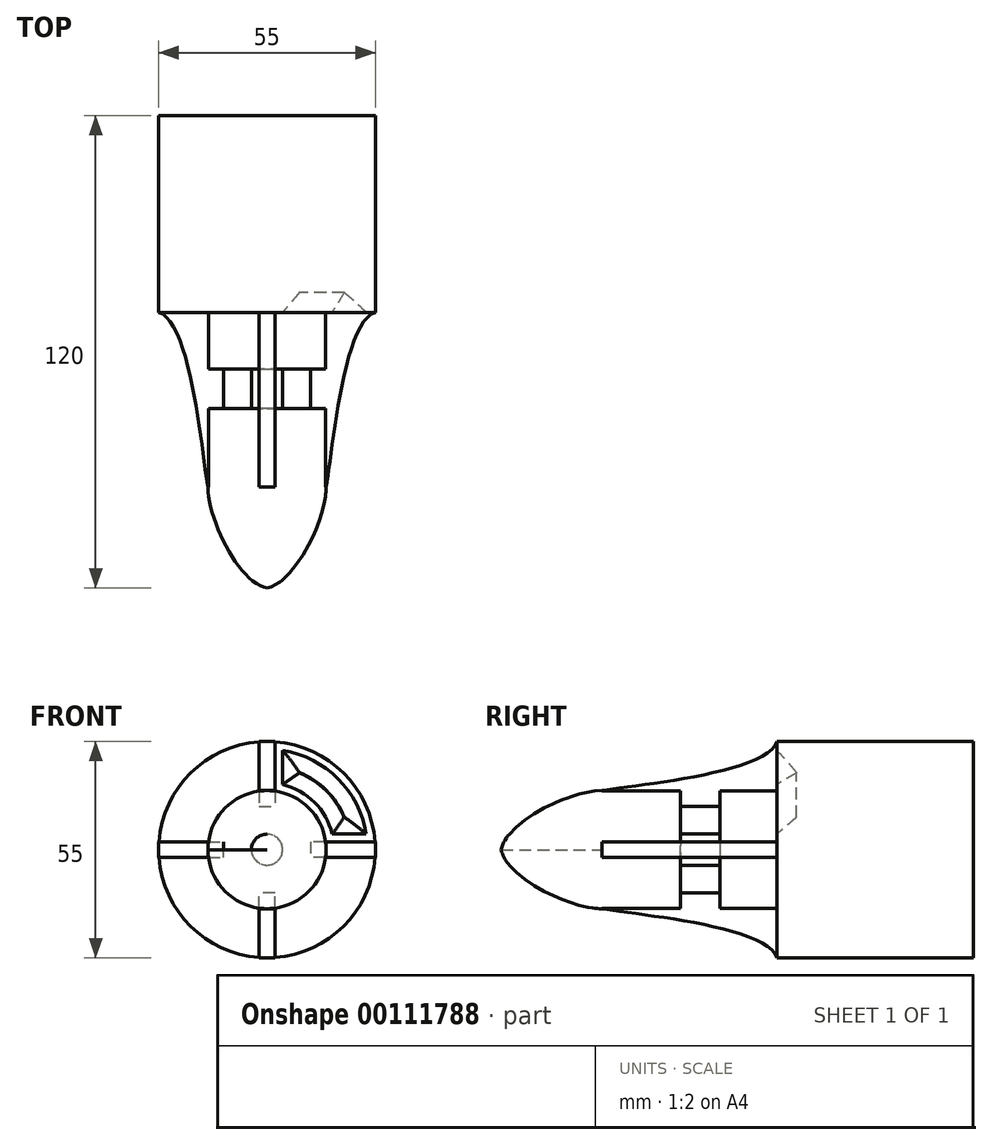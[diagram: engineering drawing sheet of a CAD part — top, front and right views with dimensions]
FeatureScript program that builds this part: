
annotation { "Feature Type Name" : "Feature", "Feature Type Description" : "" }
export const myFeature = defineFeature(function(context is Context, id is Id, definition is map)
    precondition{}
    {
        {
            var Q0;
            Q0=qCreatedBy(makeId("Front.planeOp"),FACE);
            var sketch = newSketch(context, id + "F0", { "sketchPlane" : qUnion([Q0])});
            skCircle(sketch, "E0", {"center": v(0, 0) * mm, "radius": 27.5 * mm});
            skSolve(sketch);
        }
        {
            assignVariable(context, id + "F1", {"name" : "Length", "anyValue" : 50});
        }
        {
            var Q0;
            Q0=makeQuery(id+"F0.imprint","IMPRINT",FACE,{"disambiguationData":[TD([[makeQuery(id+"F0.imprint","IMPRINT",EDGE,{"derivedFrom":sQuery(id+"F0.wireOp",EDGE,"E0")}),1.0]])]});
            extrude(context, id + "F2", {"entities" : qUnion([Q0]), "depth" : (getVariable(context, 'Length')) * mm});
        }
        {
            var Q0;
            Q0=qCreatedBy(makeId("Top.planeOp"),FACE);
            var sketch = newSketch(context, id + "F3", { "sketchPlane" : qUnion([Q0])});
            skLineSegment(sketch, "E1.0", {"start": v(27.5, -50) * mm, "end": v(-27.5, -50) * mm});
            skLineSegment(sketch, "E2", {"start": v(0, -50) * mm, "end": v(0, -120) * mm});
            skLineSegment(sketch, "E3", {"start": v(0, -50) * mm, "end": v(-15, -50) * mm});
            skLineSegment(sketch, "E4", {"start": v(-15, -50) * mm, "end": v(-15, -94.42) * mm});
            skFitSpline(sketch, "E5", {"points": [v(0, -120) * mm, v(-15, -94.42) * mm], "startDerivative": vector(-20.5, 3.36) * mm, "endDerivative": vector(0, 25.93) * mm});
            skLineSegment(sketch, "E6.bottom", {"start": v(-15, -74.42) * mm, "end": v(-3.95, -74.42) * mm});
            skLineSegment(sketch, "E6.top", {"start": v(-15, -64.42) * mm, "end": v(-3.95, -64.42) * mm});
            skLineSegment(sketch, "E6.left", {"start": v(-15, -74.42) * mm, "end": v(-15, -64.42) * mm});
            skLineSegment(sketch, "E6.right", {"start": v(-3.95, -74.42) * mm, "end": v(-3.95, -64.42) * mm});
            skSolve(sketch);
        }
        {
            var Q0;
            Q0=makeQuery(id+"F3.imprint","IMPRINT",FACE,{"disambiguationData":[TD([[makeQuery(id+"F3.imprint","IMPRINT",EDGE,{"derivedFrom":sQuery(id+"F3.wireOp",EDGE,"E2")}),-1.0]])]});
            var Q1;
            Q1=sQuery(id+"F3.wireOp",EDGE,"E2");
            revolve(context, id + "F4", {"operationType" : NewBodyOperationType.ADD, "entities" : qUnion([Q0]), "axis" : qUnion([Q1]), "revolveType" : RevolveType.FULL});
        }
        {
            var Q0;
            Q0=qCreatedBy(makeId("Top.planeOp"),FACE);
            var sketch = newSketch(context, id + "F5", { "sketchPlane" : qUnion([Q0])});
            skLineSegment(sketch, "E7.0", {"start": v(27.5, -50) * mm, "end": v(-27.5, -50) * mm});
            skFitSpline(sketch, "E8", {"points": [v(15, -94.42) * mm, v(27.5, -50) * mm], "startDerivative": vector(4.8, 26.34) * mm, "endDerivative": vector(24.57, 6.98) * mm});
            skLineSegment(sketch, "E9.0", {"start": v(-15, -94.42) * mm, "end": v(15, -94.42) * mm});
            skLineSegment(sketch, "E10.bottom", {"start": v(15, -94.42) * mm, "end": v(11, -94.42) * mm});
            skLineSegment(sketch, "E10.right", {"start": v(11, -94.42) * mm, "end": v(11, -50) * mm});
            skLineSegment(sketch, "E11", {"start": v(11, -50) * mm, "end": v(27.5, -50) * mm});
            skSolve(sketch);
        }
        {
            var Q0;
            Q0=makeQuery(id+"F5.imprint","IMPRINT",FACE,{"disambiguationData":[TD([[makeQuery(id+"F5.imprint","IMPRINT",EDGE,{"derivedFrom":sQuery(id+"F5.wireOp",EDGE,"E8")}),1.0]])]});
            extrude(context, id + "F6", {"entities" : qUnion([Q0]), "operationType" : NewBodyOperationType.ADD, "depth" : 2 * mm, "hasSecondDirection" : true, "secondDirectionOppositeDirection" : true, "secondDirectionDepth" : 2 * mm});
        }
        {
            var Q0;
            Q0=makeQuery(id+"F2.opExtrude","SWEPT_BODY",BODY,{"disambiguationData":[OSD([sQuery(id+"F0.wireOp",EDGE,"E0")])]});
            var Q1;
            Q1=makeQuery(id+"F2.opExtrude","SWEPT_FACE",FACE,{"disambiguationData":[OSD([sQuery(id+"F0.wireOp",EDGE,"E0")])]});
            circularPattern(context, id + "F7", {"operationType" : NewBodyOperationType.ADD, "entities" : qUnion([Q0]), "axis" : qUnion([Q1]), "angle" : 360 * degree, "instanceCount" : 4, "equalSpace" : true});
        }
        {
            var Q0;
            {var subQ0=sQuery(id+"F5.wireOp",EDGE,"E11");var subQ2=sQuery(id+"F5.wireOp",EDGE,"E10.right");var subQ3=sQuery(id+"F5.wireOp",EDGE,"E10.bottom");var subQ4=sQuery(id+"F5.wireOp",EDGE,"E8");var subQ6=sQuery(id+"F0.wireOp",EDGE,"E0");var subQ9=makeQuery(id+"F2.opExtrude","CAP_FACE",FACE,{"disambiguationData":[OSD([subQ6])],"isStart":false});Q0=makeQuery(id+"F7.boolean.opBoolean","SPLIT",FACE,{"disambiguationData":[TD([makeQuery(id+"F6.opExtrude","CAP_FACE",FACE,{"disambiguationData":[OSD([subQ4,subQ3,subQ2,subQ0])],"isStart":false})])],"derivedFrom":subQ9});}
            var sketch = newSketch(context, id + "F8", { "sketchPlane" : qUnion([Q0])});
            skLineSegment(sketch, "E12.0.0", {"start": v(2, 27.43) * mm, "end": v(2, 14.87) * mm});
            skArc(sketch, "E12.0.1", {"start": v(2, 14.87) * mm, "mid": v(10.6, 10.6) * mm, "end": v(14.87, 2) * mm});
            skLineSegment(sketch, "E12.0.2", {"start": v(14.87, 2) * mm, "end": v(27.43, 2) * mm});
            skArc(sketch, "E12.0.3", {"start": v(27.43, 2) * mm, "mid": v(19.45, 19.45) * mm, "end": v(2, 27.43) * mm});
            skLineSegment(sketch, "E13.0", {"start": v(4, 25.18) * mm, "end": v(4, 16.52) * mm});
            skArc(sketch, "E13.1", {"start": v(25.18, 4) * mm, "mid": v(18.03, 18.03) * mm, "end": v(4, 25.18) * mm});
            skLineSegment(sketch, "E13.2", {"start": v(16.52, 4) * mm, "end": v(25.18, 4) * mm});
            skArc(sketch, "E13.3", {"start": v(4, 16.52) * mm, "mid": v(12.02, 12.02) * mm, "end": v(16.52, 4) * mm});
            skArc(sketch, "E14.1.0", {"start": v(-16.52, 4) * mm, "mid": v(-12.02, 12.02) * mm, "end": v(-4, 16.52) * mm});
            skLineSegment(sketch, "E14.1.1", {"start": v(-4, 16.52) * mm, "end": v(-4, 25.18) * mm});
            skArc(sketch, "E14.1.2", {"start": v(-4, 25.18) * mm, "mid": v(-18.03, 18.03) * mm, "end": v(-25.18, 4) * mm});
            skLineSegment(sketch, "E14.1.3", {"start": v(-25.18, 4) * mm, "end": v(-16.52, 4) * mm});
            skArc(sketch, "E14.2.0", {"start": v(-4, -16.52) * mm, "mid": v(-12.02, -12.02) * mm, "end": v(-16.52, -4) * mm});
            skLineSegment(sketch, "E14.2.1", {"start": v(-16.52, -4) * mm, "end": v(-25.18, -4) * mm});
            skArc(sketch, "E14.2.2", {"start": v(-25.18, -4) * mm, "mid": v(-18.03, -18.03) * mm, "end": v(-4, -25.18) * mm});
            skLineSegment(sketch, "E14.2.3", {"start": v(-4, -25.18) * mm, "end": v(-4, -16.52) * mm});
            skArc(sketch, "E14.3.0", {"start": v(16.52, -4) * mm, "mid": v(12.02, -12.02) * mm, "end": v(4, -16.52) * mm});
            skLineSegment(sketch, "E14.3.1", {"start": v(4, -16.52) * mm, "end": v(4, -25.18) * mm});
            skArc(sketch, "E14.3.2", {"start": v(4, -25.18) * mm, "mid": v(18.03, -18.03) * mm, "end": v(25.18, -4) * mm});
            skLineSegment(sketch, "E14.3.3", {"start": v(25.18, -4) * mm, "end": v(16.52, -4) * mm});
            skSolve(sketch);
        }
        {
            var Q0;
            Q0=makeQuery(id+"F8.imprint","IMPRINT",FACE,{"disambiguationData":[TD([[makeQuery(id+"F8.imprint","IMPRINT",EDGE,{"derivedFrom":sQuery(id+"F8.wireOp",EDGE,"E14.3.0")}),1.0]])]});
            var Q1;
            Q1=makeQuery(id+"F8.imprint","IMPRINT",FACE,{"disambiguationData":[TD([[makeQuery(id+"F8.imprint","IMPRINT",EDGE,{"derivedFrom":sQuery(id+"F8.wireOp",EDGE,"E14.2.0")}),1.0]])]});
            var Q2;
            Q2=makeQuery(id+"F8.imprint","IMPRINT",FACE,{"disambiguationData":[TD([[makeQuery(id+"F8.imprint","IMPRINT",EDGE,{"derivedFrom":sQuery(id+"F8.wireOp",EDGE,"E13.0")}),1.0]])]});
            var Q3;
            Q3=makeQuery(id+"F8.imprint","IMPRINT",FACE,{"disambiguationData":[TD([[makeQuery(id+"F8.imprint","IMPRINT",EDGE,{"derivedFrom":sQuery(id+"F8.wireOp",EDGE,"E14.1.0")}),1.0]])]});
            extrude(context, id + "F9", {"entities" : qUnion([Q0, Q1, Q2, Q3]), "operationType" : NewBodyOperationType.REMOVE, "oppositeDirection" : true, "depth" : 5 * mm, "hasDraft" : true, "draftAngle" : 40 * degree, "draftPullDirection" : true});
        }
    });
